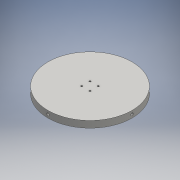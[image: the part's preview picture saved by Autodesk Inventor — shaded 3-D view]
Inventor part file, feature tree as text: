
AUTODESK INVENTOR PART (.ipt)
format: ipt  version: 2016 (Build 200138000, 138)  size: 143,872 bytes
history: native  units: mm
features: thread x8, extrude x6, sketch x6, other x5
ambient origin geometry x8: Origin, YZ Plane, XZ Plane, XY Plane, X Axis, Y Axis, Z Axis, Center Point
bodies: Body1 (feature_tree)
feature tree (25):
  other  "ソリッド1"
  extrude  "押し出し1"  Depth=101.0mm
  extrude  "押し出し2"  Depth=8.0mm TaperAngle=0.0deg
  other  "作業平面1"
  other  "作業平面2"
  other  "作業平面3"
  other  "作業平面4"
  extrude  "押し出し3"  Depth=10.0mm
  extrude  "押し出し4"  Depth=10.0mm
  extrude  "押し出し5"  Depth=2.0mm
  extrude  "押し出し6"  Depth=2.0mm
  thread  "ねじ1"
  thread  "ねじ2"
  thread  "ねじ3"
  thread  "ねじ4"
  thread  "ねじ5"
  thread  "ねじ6"
  thread  "ねじ7"
  thread  "ねじ8"
  sketch  "スケッチ1"
  sketch  "スケッチ2"
  sketch  "スケッチ3"
  sketch  "スケッチ4"
  sketch  "スケッチ5"
  sketch  "スケッチ6"
